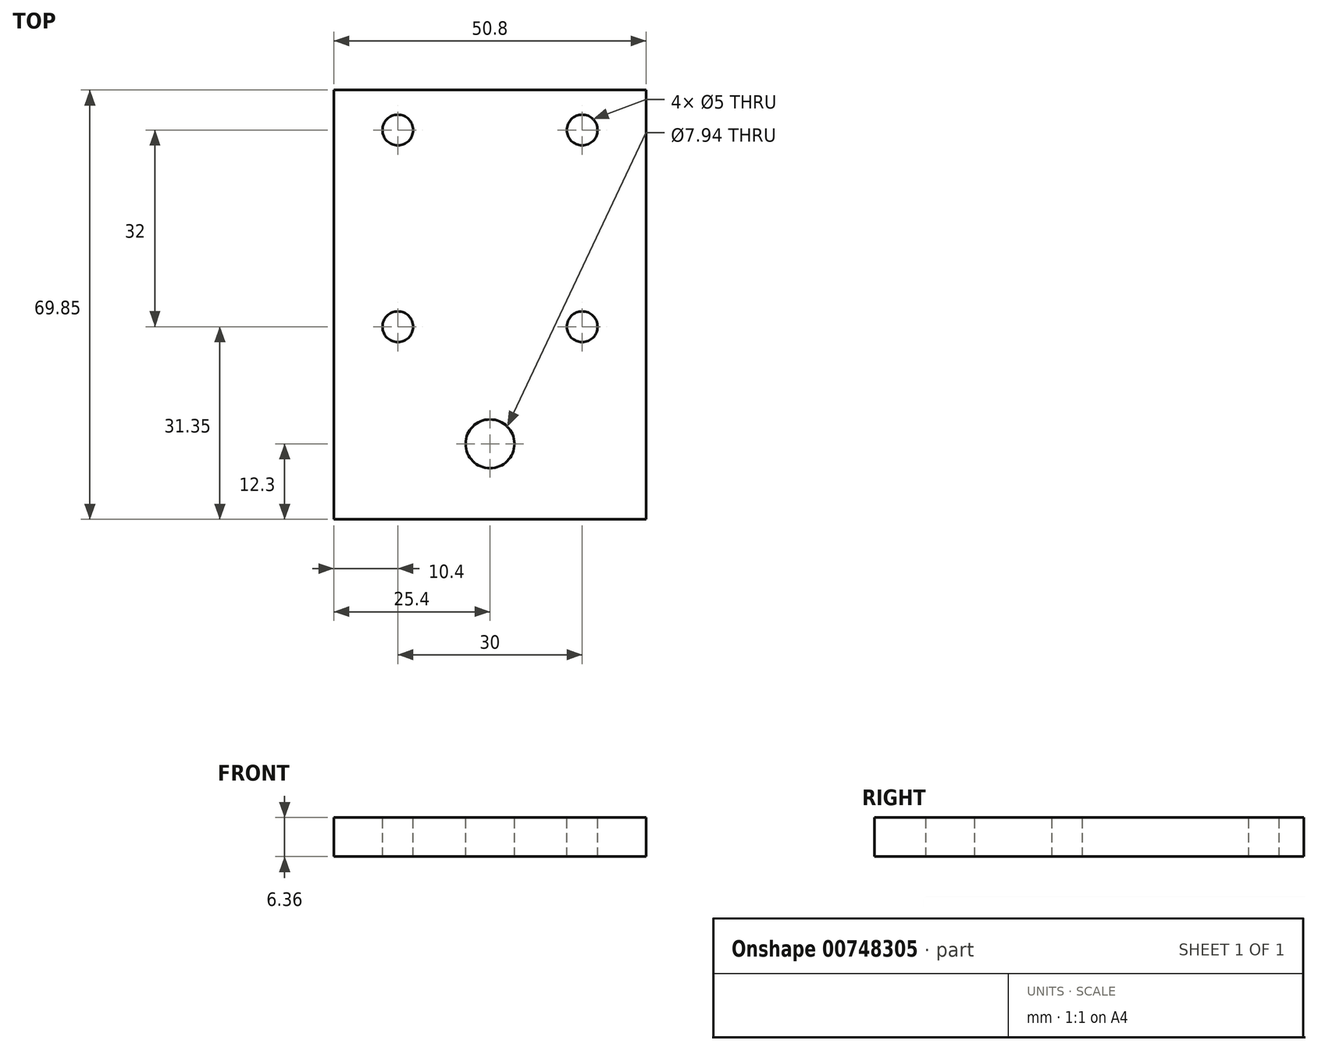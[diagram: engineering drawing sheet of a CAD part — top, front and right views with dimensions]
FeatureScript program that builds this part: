
annotation { "Feature Type Name" : "Feature", "Feature Type Description" : "" }
export const myFeature = defineFeature(function(context is Context, id is Id, definition is map)
    precondition{}
    {
        {
            var Q0;
            Q0=qCreatedBy(makeId("Front.planeOp"),FACE);
            var sketch = newSketch(context, id + "F0", { "sketchPlane" : qUnion([Q0])});
            skLineSegment(sketch, "E0.bottom", {"start": v(25.4, 3.18) * mm, "end": v(-25.4, 3.18) * mm});
            skLineSegment(sketch, "E0.top", {"start": v(25.4, -3.17) * mm, "end": v(-25.4, -3.17) * mm});
            skLineSegment(sketch, "E0.left", {"start": v(25.4, 3.18) * mm, "end": v(25.4, -3.17) * mm});
            skLineSegment(sketch, "E0.right", {"start": v(-25.4, 3.18) * mm, "end": v(-25.4, -3.17) * mm});
            skPoint(sketch, "E0.middle", {"position": v(0, 0) * mm});
            skSolve(sketch);
        }
        {
            var Q0;
            Q0=qSketchRegion(id+"F0",true);
            extrude(context, id + "F1", {"entities" : qUnion([Q0]), "depth" : 69.85 * mm, "offsetDistance" : 25.4 * mm});
        }
        {
            var Q0;
            Q0=makeQuery(id+"F1.opExtrude","SWEPT_FACE",FACE,{"disambiguationData":[OSD([sQuery(id+"F0.wireOp",EDGE,"E0.bottom")])]});
            var sketch = newSketch(context, id + "F2", { "sketchPlane" : qUnion([Q0])});
            skLineSegment(sketch, "E1", {"start": v(0, -69.85) * mm, "end": v(0, 0) * mm, "construction": true});
            skLineSegment(sketch, "E2", {"start": v(-25.4, -22.5) * mm, "end": v(25.4, -22.5) * mm, "construction": true});
            skLineSegment(sketch, "E3.0", {"start": v(-25.4, -38.5) * mm, "end": v(25.4, -38.5) * mm, "construction": true});
            skLineSegment(sketch, "E4.0", {"start": v(-25.4, -6.5) * mm, "end": v(25.4, -6.5) * mm, "construction": true});
            skLineSegment(sketch, "E5.0", {"start": v(15, -69.85) * mm, "end": v(15, 31.75) * mm, "construction": true});
            skLineSegment(sketch, "E6.0", {"start": v(-15, -69.85) * mm, "end": v(-15, 31.75) * mm, "construction": true});
            skCircle(sketch, "E7", {"center": v(-15, -38.5) * mm, "radius": 2.5 * mm});
            skCircle(sketch, "E8", {"center": v(15, -38.5) * mm, "radius": 2.5 * mm});
            skCircle(sketch, "E9", {"center": v(15, -6.5) * mm, "radius": 2.5 * mm});
            skCircle(sketch, "E10", {"center": v(-15, -6.5) * mm, "radius": 2.5 * mm});
            skPoint(sketch, "E11.middle", {"position": v(0, -34.93) * mm});
            skCircle(sketch, "E12", {"center": v(0, -57.55) * mm, "radius": 3.97 * mm});
            skSolve(sketch);
        }
        {
            var Q0;
            Q0=qSketchRegion(id+"F2",true);
            extrude(context, id + "F3", {"entities" : qUnion([Q0]), "operationType" : NewBodyOperationType.REMOVE, "endBound" : BoundingType.THROUGH_ALL, "oppositeDirection" : true, "depth" : 25.4 * mm, "offsetDistance" : 25.4 * mm});
        }
    });
